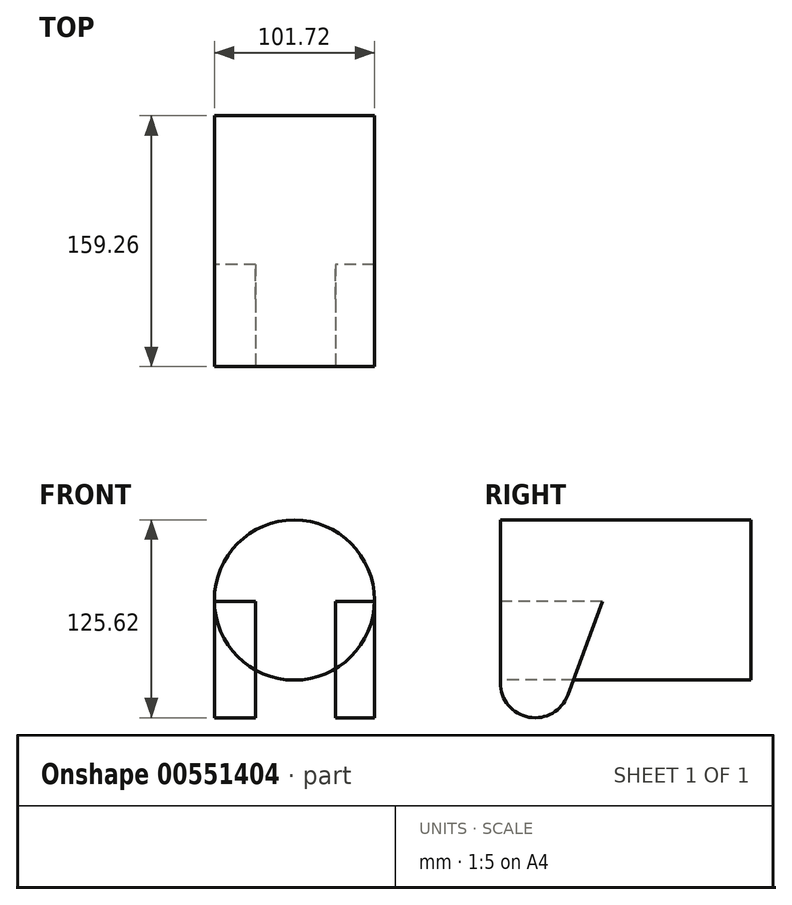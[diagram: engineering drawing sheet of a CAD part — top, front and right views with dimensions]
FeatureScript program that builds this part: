
annotation { "Feature Type Name" : "Feature", "Feature Type Description" : "" }
export const myFeature = defineFeature(function(context is Context, id is Id, definition is map)
    precondition{}
    {
        {
            var Q0;
            Q0=qCreatedBy(makeId("Right.planeOp"),FACE);
            var sketch = newSketch(context, id + "F0", { "sketchPlane" : qUnion([Q0])});
            skLineSegment(sketch, "E0", {"start": v(0, -11.32) * mm, "end": v(0, 40.34) * mm});
            skLineSegment(sketch, "E1", {"start": v(0, 40.34) * mm, "end": v(64.83, 40.34) * mm});
            skLineSegment(sketch, "E2", {"start": v(64.83, 40.34) * mm, "end": v(42.83, -19) * mm});
            skArc(sketch, "E3", {"start": v(42.83, -19) * mm, "mid": v(18.2, -33.07) * mm, "end": v(0, -11.32) * mm});
            skSolve(sketch);
        }
        {
            var Q0;
            Q0 = qSketchRegion(id + "F0", true);
            extrude(context, id + "F1", {"entities" : qUnion([Q0]), "endBound" : BoundingType.SYMMETRIC, "depth" : 101.6 * mm, "offsetDistance" : 25.4 * mm});
        }
        {
            var Q0;
            Q0=qCreatedBy(makeId("Front.planeOp"),FACE);
            var sketch = newSketch(context, id + "F2", { "sketchPlane" : qUnion([Q0])});
            skLineSegment(sketch, "E4.bottom", {"start": v(-24.57, 40.46) * mm, "end": v(26.23, 40.46) * mm});
            skLineSegment(sketch, "E4.top", {"start": v(-24.57, -33.7) * mm, "end": v(26.23, -33.7) * mm});
            skLineSegment(sketch, "E4.left", {"start": v(-24.57, 40.46) * mm, "end": v(-24.57, -33.7) * mm});
            skLineSegment(sketch, "E4.right", {"start": v(26.23, 40.46) * mm, "end": v(26.23, -33.7) * mm});
            skSolve(sketch);
        }
        {
            var Q0;
            Q0=makeQuery(id+"F2.imprint","IMPRINT",FACE,{"disambiguationData":[TD([[makeQuery(id+"F2.imprint","IMPRINT",EDGE,{"derivedFrom":sQuery(id+"F2.wireOp",EDGE,"E4.bottom")}),-1.0]])]});
            extrude(context, id + "F3", {"entities" : qUnion([Q0]), "operationType" : NewBodyOperationType.REMOVE, "oppositeDirection" : true, "depth" : 170.7 * mm, "offsetDistance" : 25.4 * mm});
        }
        {
            var Q0;
            Q0=qCreatedBy(makeId("Front.planeOp"),FACE);
            var sketch = newSketch(context, id + "F4", { "sketchPlane" : qUnion([Q0])});
            skCircle(sketch, "E5", {"center": v(0, 41.34) * mm, "radius": 50.86 * mm});
            skSolve(sketch);
        }
        {
            var Q0;
            Q0=makeQuery(id+"F4.imprint","IMPRINT",FACE,{"disambiguationData":[TD([[makeQuery(id+"F4.imprint","IMPRINT",EDGE,{"derivedFrom":sQuery(id+"F4.wireOp",EDGE,"E5")}),1.0]])]});
            extrude(context, id + "F5", {"entities" : qUnion([Q0]), "oppositeDirection" : true, "depth" : 159.26 * mm, "offsetDistance" : 25.4 * mm});
        }
    });
